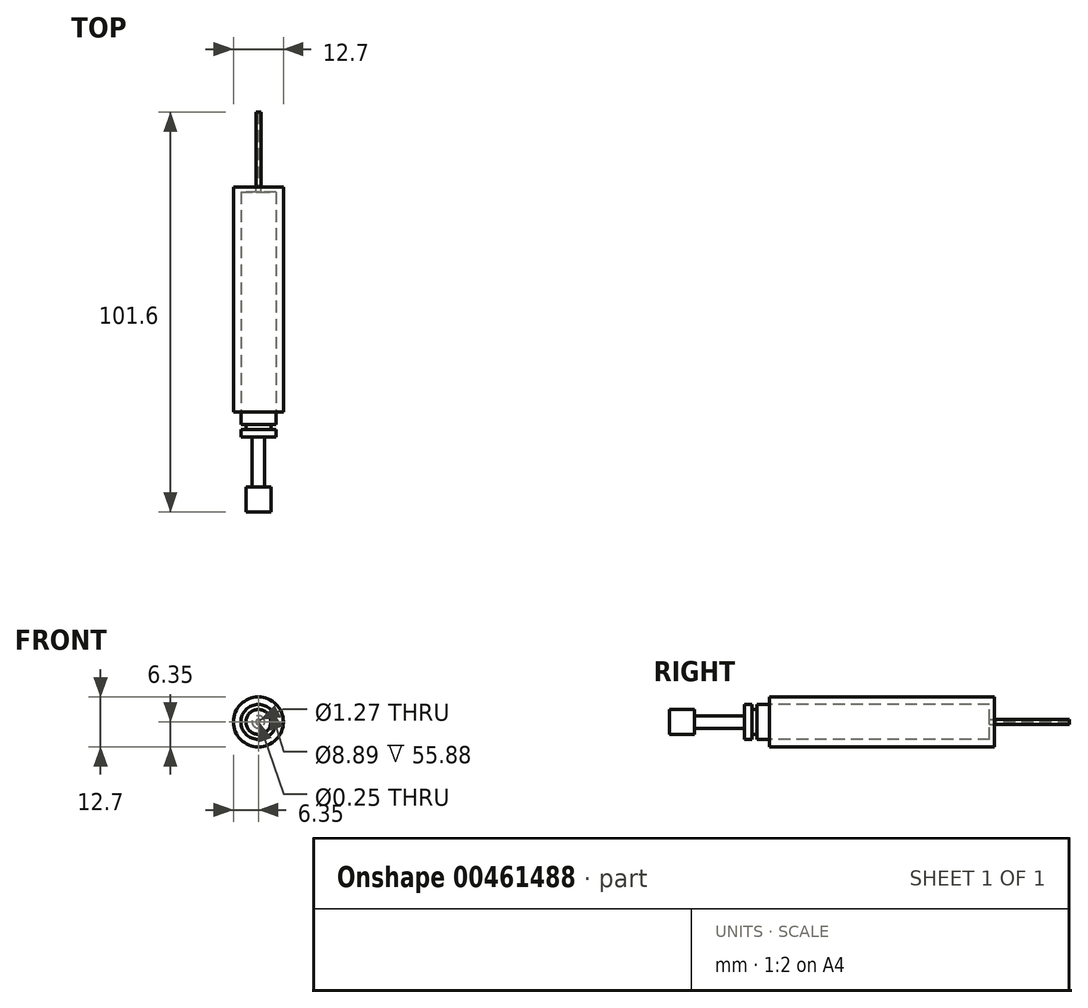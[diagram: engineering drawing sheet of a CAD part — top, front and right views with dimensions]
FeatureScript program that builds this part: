
annotation { "Feature Type Name" : "Feature", "Feature Type Description" : "" }
export const myFeature = defineFeature(function(context is Context, id is Id, definition is map)
    precondition{}
    {
        {
            var Q0;
            Q0=qCreatedBy(makeId("Front.planeOp"),FACE);
            var sketch = newSketch(context, id + "F0", { "sketchPlane" : qUnion([Q0])});
            skCircle(sketch, "E0", {"center": v(0, 0) * mm, "radius": 0.64 * mm});
            skSolve(sketch);
        }
        {
            var Q0;
            Q0=makeQuery(id+"F0.imprint","IMPRINT",FACE,{"disambiguationData":[TD([[makeQuery(id+"F0.imprint","IMPRINT",EDGE,{"derivedFrom":sQuery(id+"F0.wireOp",EDGE,"E0")}),1.0]])]});
            extrude(context, id + "F1", {"entities" : qUnion([Q0]), "depth" : 19.05 * mm});
        }
        {
            var Q0;
            Q0=makeQuery(id+"F1.opExtrude","CAP_FACE",FACE,{"disambiguationData":[OSD([sQuery(id+"F0.wireOp",EDGE,"E0")])],"isStart":false});
            var sketch = newSketch(context, id + "F2", { "sketchPlane" : qUnion([Q0])});
            skCircle(sketch, "E1", {"center": v(0, 0) * mm, "radius": 0.13 * mm});
            skSolve(sketch);
        }
        {
            var Q0;
            Q0=makeQuery(id+"F2.imprint","IMPRINT",FACE,{"disambiguationData":[TD([[makeQuery(id+"F2.imprint","IMPRINT",EDGE,{"derivedFrom":sQuery(id+"F2.wireOp",EDGE,"E1")}),1.0]])]});
            extrude(context, id + "F3", {"entities" : qUnion([Q0]), "operationType" : NewBodyOperationType.REMOVE, "oppositeDirection" : true, "depth" : 25.4 * mm});
        }
        {
            var Q0;
            Q0=makeQuery(id+"F1.opExtrude","CAP_FACE",FACE,{"disambiguationData":[OSD([sQuery(id+"F0.wireOp",EDGE,"E0")])],"isStart":false});
            var sketch = newSketch(context, id + "F4", { "sketchPlane" : qUnion([Q0])});
            skCircle(sketch, "E2", {"center": v(0, 0) * mm, "radius": 6.35 * mm});
            skSolve(sketch);
        }
        {
            var Q0;
            Q0=makeQuery(id+"F4.imprint","IMPRINT",FACE,{"disambiguationData":[TD([[makeQuery(id+"F4.imprint","IMPRINT",EDGE,{"derivedFrom":sQuery(id+"F4.wireOp",EDGE,"E2")}),1.0]])]});
            extrude(context, id + "F5", {"entities" : qUnion([Q0]), "depth" : 57.15 * mm});
        }
        {
            var Q0;
            Q0=makeQuery(id+"F5.opExtrude","CAP_FACE",FACE,{"disambiguationData":[OSD([sQuery(id+"F0.wireOp",EDGE,"E0"),sQuery(id+"F4.wireOp",EDGE,"E2")])],"isStart":false});
            var sketch = newSketch(context, id + "F6", { "sketchPlane" : qUnion([Q0])});
            skCircle(sketch, "E3", {"center": v(0, 0) * mm, "radius": 4.45 * mm});
            skSolve(sketch);
        }
        {
            var Q0;
            Q0=makeQuery(id+"F6.imprint","IMPRINT",FACE,{"disambiguationData":[TD([[makeQuery(id+"F6.imprint","IMPRINT",EDGE,{"derivedFrom":sQuery(id+"F6.wireOp",EDGE,"E3")}),1.0]])]});
            extrude(context, id + "F7", {"entities" : qUnion([Q0]), "operationType" : NewBodyOperationType.REMOVE, "oppositeDirection" : true, "depth" : 55.88 * mm});
        }
        {
            var Q0;
            Q0=makeQuery(id+"F5.opExtrude","CAP_FACE",FACE,{"disambiguationData":[OSD([sQuery(id+"F0.wireOp",EDGE,"E0"),sQuery(id+"F4.wireOp",EDGE,"E2")])],"isStart":false});
            var sketch = newSketch(context, id + "F8", { "sketchPlane" : qUnion([Q0])});
            skCircle(sketch, "E4", {"center": v(0, 0) * mm, "radius": 4.45 * mm});
            skSolve(sketch);
        }
        {
            var Q0;
            Q0=makeQuery(id+"F8.imprint","IMPRINT",FACE,{"disambiguationData":[TD([[makeQuery(id+"F8.imprint","IMPRINT",EDGE,{"derivedFrom":sQuery(id+"F8.wireOp",EDGE,"E4")}),1.0]])]});
            extrude(context, id + "F9", {"entities" : qUnion([Q0]), "depth" : 3.17 * mm});
        }
        {
            var Q0;
            Q0=makeQuery(id+"F9.opExtrude","CAP_FACE",FACE,{"disambiguationData":[OSD([sQuery(id+"F8.wireOp",EDGE,"E4")])],"isStart":false});
            var sketch = newSketch(context, id + "F10", { "sketchPlane" : qUnion([Q0])});
            skCircle(sketch, "E5", {"center": v(0, 0) * mm, "radius": 3.18 * mm});
            skSolve(sketch);
        }
        {
            var Q0;
            Q0=makeQuery(id+"F10.imprint","IMPRINT",FACE,{"disambiguationData":[TD([[makeQuery(id+"F10.imprint","IMPRINT",EDGE,{"derivedFrom":sQuery(id+"F10.wireOp",EDGE,"E5")}),1.0]])]});
            extrude(context, id + "F11", {"entities" : qUnion([Q0]), "operationType" : NewBodyOperationType.ADD, "depth" : 1.27 * mm});
        }
        {
            var Q0;
            Q0=makeQuery(id+"F11.opExtrude","CAP_FACE",FACE,{"disambiguationData":[OSD([sQuery(id+"F10.wireOp",EDGE,"E5")])],"isStart":false});
            var sketch = newSketch(context, id + "F12", { "sketchPlane" : qUnion([Q0])});
            skCircle(sketch, "E6", {"center": v(0, 0) * mm, "radius": 4.45 * mm});
            skSolve(sketch);
        }
        {
            var Q0;
            Q0=makeQuery(id+"F12.imprint","IMPRINT",FACE,{"disambiguationData":[TD([[makeQuery(id+"F12.imprint","IMPRINT",EDGE,{"derivedFrom":sQuery(id+"F12.wireOp",EDGE,"E6")}),1.0]])]});
            var Q1;
            Q1=makeQuery(id+"F12.imprint","IMPRINT",FACE,{"disambiguationData":[TD([[makeQuery(id+"F12.imprint","IMPRINT",EDGE,{"derivedFrom":makeQuery(id+"F11.opExtrude","CAP_EDGE",EDGE,{"disambiguationData":[OSD([sQuery(id+"F10.wireOp",EDGE,"E5")])],"isStart":false})}),1.0]])]});
            extrude(context, id + "F13", {"entities" : qUnion([Q0, Q1]), "operationType" : NewBodyOperationType.ADD, "depth" : 1.9 * mm});
        }
        {
            var Q0;
            Q0=makeQuery(id+"F13.opExtrude","CAP_FACE",FACE,{"disambiguationData":[OSD([sQuery(id+"F12.wireOp",EDGE,"E6")])],"isStart":false});
            var sketch = newSketch(context, id + "F14", { "sketchPlane" : qUnion([Q0])});
            skCircle(sketch, "E7", {"center": v(0, 0) * mm, "radius": 1.59 * mm});
            skSolve(sketch);
        }
        {
            var Q0;
            Q0=makeQuery(id+"F14.imprint","IMPRINT",FACE,{"disambiguationData":[TD([[makeQuery(id+"F14.imprint","IMPRINT",EDGE,{"derivedFrom":sQuery(id+"F14.wireOp",EDGE,"E7")}),1.0]])]});
            extrude(context, id + "F15", {"entities" : qUnion([Q0]), "operationType" : NewBodyOperationType.ADD, "depth" : 12.7 * mm});
        }
        {
            var Q0;
            Q0=makeQuery(id+"F15.opExtrude","CAP_FACE",FACE,{"disambiguationData":[OSD([sQuery(id+"F14.wireOp",EDGE,"E7")])],"isStart":false});
            var sketch = newSketch(context, id + "F16", { "sketchPlane" : qUnion([Q0])});
            skCircle(sketch, "E8", {"center": v(0, 0) * mm, "radius": 3.18 * mm});
            skSolve(sketch);
        }
        {
            var Q0;
            Q0=makeQuery(id+"F16.imprint","IMPRINT",FACE,{"disambiguationData":[TD([[makeQuery(id+"F16.imprint","IMPRINT",EDGE,{"derivedFrom":sQuery(id+"F16.wireOp",EDGE,"E8")}),1.0]])]});
            var Q1;
            Q1=makeQuery(id+"F16.imprint","IMPRINT",FACE,{"disambiguationData":[TD([[makeQuery(id+"F16.imprint","IMPRINT",EDGE,{"derivedFrom":makeQuery(id+"F15.opExtrude","CAP_EDGE",EDGE,{"disambiguationData":[OSD([sQuery(id+"F14.wireOp",EDGE,"E7")])],"isStart":false})}),1.0]])]});
            extrude(context, id + "F17", {"entities" : qUnion([Q0, Q1]), "depth" : 6.35 * mm});
        }
    });
